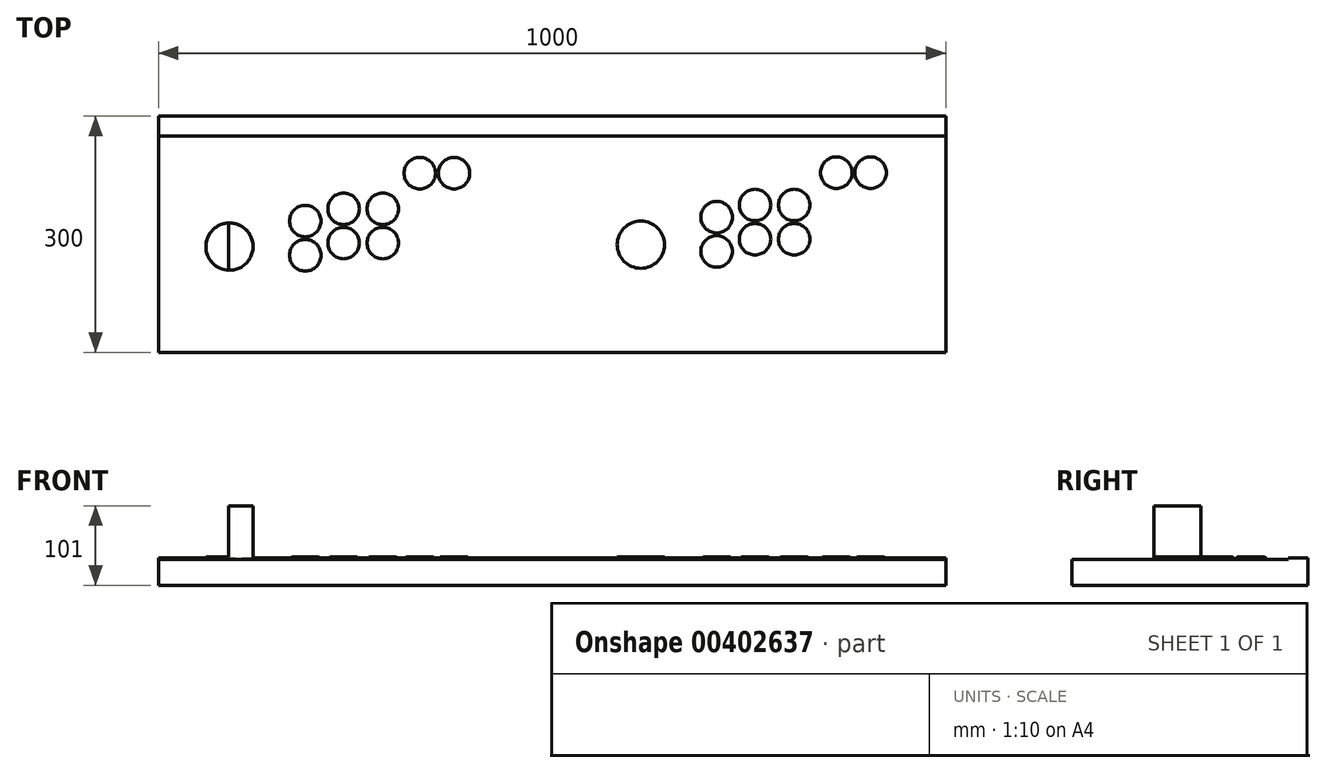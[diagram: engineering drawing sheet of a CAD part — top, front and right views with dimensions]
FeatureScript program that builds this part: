
annotation { "Feature Type Name" : "Feature", "Feature Type Description" : "" }
export const myFeature = defineFeature(function(context is Context, id is Id, definition is map)
    precondition{}
    {
        {
            var Q0;
            Q0=qCreatedBy(makeId("Front.planeOp"),FACE);
            var sketch = newSketch(context, id + "F0", { "sketchPlane" : qUnion([Q0])});
            skLineSegment(sketch, "E0.bottom", {"start": v(-84.86, 26.9) * mm, "end": v(915.14, 26.9) * mm});
            skLineSegment(sketch, "E0.top", {"start": v(-84.86, -8.1) * mm, "end": v(915.14, -8.1) * mm});
            skLineSegment(sketch, "E0.left", {"start": v(-84.86, 26.9) * mm, "end": v(-84.86, -8.1) * mm});
            skLineSegment(sketch, "E0.right", {"start": v(915.14, 26.9) * mm, "end": v(915.14, -8.1) * mm});
            skSolve(sketch);
        }
        {
            var Q0;
            Q0=makeQuery(id+"F0.imprint","IMPRINT",FACE,{"disambiguationData":[TD([[makeQuery(id+"F0.imprint","IMPRINT",EDGE,{"derivedFrom":sQuery(id+"F0.wireOp",EDGE,"E0.bottom")}),-1.0]])]});
            extrude(context, id + "F1", {"entities" : qUnion([Q0]), "depth" : 300 * mm});
        }
        {
            var Q0;
            Q0=makeQuery(id+"F1.opExtrude","SWEPT_FACE",FACE,{"disambiguationData":[OSD([sQuery(id+"F0.wireOp",EDGE,"E0.bottom")])]});
            var sketch = newSketch(context, id + "F2", { "sketchPlane" : qUnion([Q0])});
            skLineSegment(sketch, "E1", {"start": v(-84.86, 0) * mm, "end": v(-84.86, -25) * mm});
            skLineSegment(sketch, "E2", {"start": v(-84.86, -25) * mm, "end": v(915.14, -25) * mm});
            skLineSegment(sketch, "E3", {"start": v(915.14, -25) * mm, "end": v(915.14, -300) * mm});
            skLineSegment(sketch, "E4", {"start": v(915.14, -300) * mm, "end": v(-84.86, -300) * mm});
            skLineSegment(sketch, "E5", {"start": v(-84.86, -300) * mm, "end": v(-84.86, -25) * mm});
            skSolve(sketch);
        }
        {
            var Q0;
            Q0=makeQuery(id+"F2.imprint","IMPRINT",FACE,{"disambiguationData":[TD([[makeQuery(id+"F2.imprint","IMPRINT",EDGE,{"derivedFrom":sQuery(id+"F2.wireOp",EDGE,"E2")}),-1.0]])]});
            extrude(context, id + "F3", {"entities" : qUnion([Q0]), "operationType" : NewBodyOperationType.REMOVE, "oppositeDirection" : true, "depth" : 2 * mm});
        }
        {
            var Q0;
            Q0=makeQuery(id+"F3.boolean.opBoolean","COPY",FACE,{"derivedFrom":makeQuery(id+"F3.opExtrude","CAP_FACE",FACE,{"disambiguationData":[OSD([sQuery(id+"F2.wireOp",EDGE,"E2"),sQuery(id+"F2.wireOp",EDGE,"E3"),sQuery(id+"F2.wireOp",EDGE,"E4"),sQuery(id+"F2.wireOp",EDGE,"E5")])],"isStart":false})});
            var sketch = newSketch(context, id + "F4", { "sketchPlane" : qUnion([Q0])});
            skCircle(sketch, "E6", {"center": v(101.57, -133.2) * mm, "radius": 20 * mm});
            skCircle(sketch, "E7", {"center": v(101.57, -176.72) * mm, "radius": 20 * mm});
            skCircle(sketch, "E8", {"center": v(150.29, -117.7) * mm, "radius": 20 * mm});
            skCircle(sketch, "E9", {"center": v(150.29, -161.2) * mm, "radius": 20 * mm});
            skCircle(sketch, "E10", {"center": v(200.06, -117.7) * mm, "radius": 20 * mm});
            skCircle(sketch, "E11", {"center": v(200.06, -161.2) * mm, "radius": 20 * mm});
            skCircle(sketch, "E12", {"center": v(624.16, -128.32) * mm, "radius": 20 * mm});
            skCircle(sketch, "E13", {"center": v(624.16, -171.83) * mm, "radius": 20 * mm});
            skCircle(sketch, "E14", {"center": v(672.88, -112.82) * mm, "radius": 20 * mm});
            skCircle(sketch, "E15", {"center": v(672.88, -156.32) * mm, "radius": 20 * mm});
            skCircle(sketch, "E16", {"center": v(722.66, -112.82) * mm, "radius": 20 * mm});
            skCircle(sketch, "E17", {"center": v(722.66, -156.32) * mm, "radius": 20 * mm});
            skCircle(sketch, "E18", {"center": v(5.32, -165.7) * mm, "radius": 30 * mm});
            skCircle(sketch, "E19", {"center": v(527.86, -163.26) * mm, "radius": 30 * mm});
            skCircle(sketch, "E20", {"center": v(247.04, -72.43) * mm, "radius": 20 * mm});
            skCircle(sketch, "E21", {"center": v(290.54, -72.43) * mm, "radius": 20 * mm});
            skCircle(sketch, "E22", {"center": v(776.15, -71.82) * mm, "radius": 20 * mm});
            skCircle(sketch, "E23", {"center": v(819.66, -71.82) * mm, "radius": 20 * mm});
            skSolve(sketch);
        }
        {
            var Q0;
            Q0=makeQuery(id+"F4.imprint","IMPRINT",FACE,{"disambiguationData":[TD([[makeQuery(id+"F4.imprint","IMPRINT",EDGE,{"derivedFrom":sQuery(id+"F4.wireOp",EDGE,"E18")}),1.0]])]});
            var Q1;
            Q1=makeQuery(id+"F4.imprint","IMPRINT",FACE,{"disambiguationData":[TD([[makeQuery(id+"F4.imprint","IMPRINT",EDGE,{"derivedFrom":sQuery(id+"F4.wireOp",EDGE,"E7")}),1.0]])]});
            var Q2;
            Q2=makeQuery(id+"F4.imprint","IMPRINT",FACE,{"disambiguationData":[TD([[makeQuery(id+"F4.imprint","IMPRINT",EDGE,{"derivedFrom":sQuery(id+"F4.wireOp",EDGE,"E6")}),1.0]])]});
            var Q3;
            Q3=makeQuery(id+"F4.imprint","IMPRINT",FACE,{"disambiguationData":[TD([[makeQuery(id+"F4.imprint","IMPRINT",EDGE,{"derivedFrom":sQuery(id+"F4.wireOp",EDGE,"E8")}),1.0]])]});
            var Q4;
            Q4=makeQuery(id+"F4.imprint","IMPRINT",FACE,{"disambiguationData":[TD([[makeQuery(id+"F4.imprint","IMPRINT",EDGE,{"derivedFrom":sQuery(id+"F4.wireOp",EDGE,"E11")}),1.0]])]});
            var Q5;
            Q5=makeQuery(id+"F4.imprint","IMPRINT",FACE,{"disambiguationData":[TD([[makeQuery(id+"F4.imprint","IMPRINT",EDGE,{"derivedFrom":sQuery(id+"F4.wireOp",EDGE,"E10")}),1.0]])]});
            var Q6;
            Q6=makeQuery(id+"F4.imprint","IMPRINT",FACE,{"disambiguationData":[TD([[makeQuery(id+"F4.imprint","IMPRINT",EDGE,{"derivedFrom":sQuery(id+"F4.wireOp",EDGE,"E9")}),1.0]])]});
            var Q7;
            Q7=makeQuery(id+"F4.imprint","IMPRINT",FACE,{"disambiguationData":[TD([[makeQuery(id+"F4.imprint","IMPRINT",EDGE,{"derivedFrom":sQuery(id+"F4.wireOp",EDGE,"E20")}),1.0]])]});
            var Q8;
            Q8=makeQuery(id+"F4.imprint","IMPRINT",FACE,{"disambiguationData":[TD([[makeQuery(id+"F4.imprint","IMPRINT",EDGE,{"derivedFrom":sQuery(id+"F4.wireOp",EDGE,"E21")}),1.0]])]});
            var Q9;
            Q9=makeQuery(id+"F4.imprint","IMPRINT",FACE,{"disambiguationData":[TD([[makeQuery(id+"F4.imprint","IMPRINT",EDGE,{"derivedFrom":sQuery(id+"F4.wireOp",EDGE,"E19")}),1.0]])]});
            var Q10;
            Q10=makeQuery(id+"F4.imprint","IMPRINT",FACE,{"disambiguationData":[TD([[makeQuery(id+"F4.imprint","IMPRINT",EDGE,{"derivedFrom":sQuery(id+"F4.wireOp",EDGE,"E13")}),1.0]])]});
            var Q11;
            Q11=makeQuery(id+"F4.imprint","IMPRINT",FACE,{"disambiguationData":[TD([[makeQuery(id+"F4.imprint","IMPRINT",EDGE,{"derivedFrom":sQuery(id+"F4.wireOp",EDGE,"E12")}),1.0]])]});
            var Q12;
            Q12=makeQuery(id+"F4.imprint","IMPRINT",FACE,{"disambiguationData":[TD([[makeQuery(id+"F4.imprint","IMPRINT",EDGE,{"derivedFrom":sQuery(id+"F4.wireOp",EDGE,"E14")}),1.0]])]});
            var Q13;
            Q13=makeQuery(id+"F4.imprint","IMPRINT",FACE,{"disambiguationData":[TD([[makeQuery(id+"F4.imprint","IMPRINT",EDGE,{"derivedFrom":sQuery(id+"F4.wireOp",EDGE,"E15")}),1.0]])]});
            var Q14;
            Q14=makeQuery(id+"F4.imprint","IMPRINT",FACE,{"disambiguationData":[TD([[makeQuery(id+"F4.imprint","IMPRINT",EDGE,{"derivedFrom":sQuery(id+"F4.wireOp",EDGE,"E17")}),1.0]])]});
            var Q15;
            Q15=makeQuery(id+"F4.imprint","IMPRINT",FACE,{"disambiguationData":[TD([[makeQuery(id+"F4.imprint","IMPRINT",EDGE,{"derivedFrom":sQuery(id+"F4.wireOp",EDGE,"E16")}),1.0]])]});
            var Q16;
            Q16=makeQuery(id+"F4.imprint","IMPRINT",FACE,{"disambiguationData":[TD([[makeQuery(id+"F4.imprint","IMPRINT",EDGE,{"derivedFrom":sQuery(id+"F4.wireOp",EDGE,"E22")}),1.0]])]});
            var Q17;
            Q17=makeQuery(id+"F4.imprint","IMPRINT",FACE,{"disambiguationData":[TD([[makeQuery(id+"F4.imprint","IMPRINT",EDGE,{"derivedFrom":sQuery(id+"F4.wireOp",EDGE,"E23")}),1.0]])]});
            extrude(context, id + "F5", {"entities" : qUnion([Q0, Q1, Q2, Q3, Q4, Q5, Q6, Q7, Q8, Q9, Q10, Q11, Q12, Q13, Q14, Q15, Q16, Q17]), "operationType" : NewBodyOperationType.ADD, "depth" : 3 * mm});
        }
        {
            var Q0;
            Q0=makeQuery(id+"F5.opExtrude","CAP_EDGE",EDGE,{"disambiguationData":[OSD([sQuery(id+"F4.wireOp",EDGE,"E7")])],"isStart":false});
            var Q1;
            Q1=makeQuery(id+"F5.opExtrude","CAP_FACE",FACE,{"disambiguationData":[OSD([sQuery(id+"F4.wireOp",EDGE,"E6")])],"isStart":false});
            var Q2;
            Q2=makeQuery(id+"F5.opExtrude","CAP_FACE",FACE,{"disambiguationData":[OSD([sQuery(id+"F4.wireOp",EDGE,"E8")])],"isStart":false});
            var Q3;
            Q3=makeQuery(id+"F5.opExtrude","CAP_FACE",FACE,{"disambiguationData":[OSD([sQuery(id+"F4.wireOp",EDGE,"E9")])],"isStart":false});
            var Q4;
            Q4=makeQuery(id+"F5.opExtrude","CAP_FACE",FACE,{"disambiguationData":[OSD([sQuery(id+"F4.wireOp",EDGE,"E11")])],"isStart":false});
            var Q5;
            Q5=makeQuery(id+"F5.opExtrude","CAP_FACE",FACE,{"disambiguationData":[OSD([sQuery(id+"F4.wireOp",EDGE,"E10")])],"isStart":false});
            var Q6;
            Q6=makeQuery(id+"F5.opExtrude","CAP_FACE",FACE,{"disambiguationData":[OSD([sQuery(id+"F4.wireOp",EDGE,"E20")])],"isStart":false});
            var Q7;
            Q7=makeQuery(id+"F5.opExtrude","CAP_FACE",FACE,{"disambiguationData":[OSD([sQuery(id+"F4.wireOp",EDGE,"E21")])],"isStart":false});
            var Q8;
            Q8=makeQuery(id+"F5.opExtrude","CAP_FACE",FACE,{"disambiguationData":[OSD([sQuery(id+"F4.wireOp",EDGE,"E23")])],"isStart":false});
            var Q9;
            Q9=makeQuery(id+"F5.opExtrude","CAP_FACE",FACE,{"disambiguationData":[OSD([sQuery(id+"F4.wireOp",EDGE,"E22")])],"isStart":false});
            var Q10;
            Q10=makeQuery(id+"F5.opExtrude","CAP_FACE",FACE,{"disambiguationData":[OSD([sQuery(id+"F4.wireOp",EDGE,"E16")])],"isStart":false});
            var Q11;
            Q11=makeQuery(id+"F5.opExtrude","CAP_FACE",FACE,{"disambiguationData":[OSD([sQuery(id+"F4.wireOp",EDGE,"E17")])],"isStart":false});
            var Q12;
            Q12=makeQuery(id+"F5.opExtrude","CAP_FACE",FACE,{"disambiguationData":[OSD([sQuery(id+"F4.wireOp",EDGE,"E15")])],"isStart":false});
            var Q13;
            Q13=makeQuery(id+"F5.opExtrude","CAP_FACE",FACE,{"disambiguationData":[OSD([sQuery(id+"F4.wireOp",EDGE,"E14")])],"isStart":false});
            var Q14;
            Q14=makeQuery(id+"F5.opExtrude","CAP_FACE",FACE,{"disambiguationData":[OSD([sQuery(id+"F4.wireOp",EDGE,"E12")])],"isStart":false});
            var Q15;
            Q15=makeQuery(id+"F5.opExtrude","CAP_FACE",FACE,{"disambiguationData":[OSD([sQuery(id+"F4.wireOp",EDGE,"E13")])],"isStart":false});
            fillet(context, id + "F6", {"entities" : qUnion([Q0, Q1, Q2, Q3, Q4, Q5, Q6, Q7, Q8, Q9, Q10, Q11, Q12, Q13, Q14, Q15]), "radius" : 5 * mm, "tangentPropagation" : true, "allowEdgeOverflow" : false});
        }
        {
            var Q0;
            Q0=makeQuery(id+"F5.opExtrude","CAP_FACE",FACE,{"disambiguationData":[OSD([sQuery(id+"F4.wireOp",EDGE,"E18")])],"isStart":false});
            var sketch = newSketch(context, id + "F7", { "sketchPlane" : qUnion([Q0])});
            skLineSegment(sketch, "E24", {"start": v(-24.68, -165.94) * mm, "end": v(35.31, -165.94) * mm});
            skLineSegment(sketch, "E25", {"start": v(4.43, -135.7) * mm, "end": v(4.43, -195.68) * mm});
            skLineSegment(sketch, "E26", {"start": v(526.33, -132.92) * mm, "end": v(526.33, -192.14) * mm});
            skLineSegment(sketch, "E27", {"start": v(557.47, -162.22) * mm, "end": v(497.03, -162.22) * mm});
            skCircle(sketch, "E28", {"center": v(4.43, -165.94) * mm, "radius": 10 * mm});
            skCircle(sketch, "E29", {"center": v(527.25, -162.22) * mm, "radius": 10 * mm});
            skSolve(sketch);
        }
        {
            var Q0;
            {var subQ0=sQuery(id+"F7.wireOp",EDGE,"E25");var subQ1=sQuery(id+"F7.wireOp",EDGE,"E24");var subQ2=makeQuery(id+"F7.imprint","INTERSECT",VERTEX,{"derivedFrom":[subQ1,subQ0]});Q0=makeQuery(id+"F7.imprint","IMPRINT",FACE,{"disambiguationData":[TD([[makeQuery(id+"F7.imprint","IMPRINT",EDGE,{"disambiguationData":[TD([[subQ2,-1.0]])],"derivedFrom":subQ1}),-1.0]])]});}
            var Q1;
            {var subQ0=sQuery(id+"F7.wireOp",EDGE,"E28");var subQ1=sQuery(id+"F7.wireOp",EDGE,"E24");var subQ2=makeQuery(id+"F7.imprint","INTERSECT",VERTEX,{"disambiguationData":[OD(0.0)],"derivedFrom":[subQ1,subQ0]});Q1=makeQuery(id+"F7.imprint","IMPRINT",FACE,{"disambiguationData":[TD([[makeQuery(id+"F7.imprint","IMPRINT",EDGE,{"disambiguationData":[TD([[subQ2,-1.0]])],"derivedFrom":subQ1}),-1.0]])]});}
            var Q2;
            {var subQ0=sQuery(id+"F7.wireOp",EDGE,"E28");var subQ1=sQuery(id+"F7.wireOp",EDGE,"E24");var subQ2=makeQuery(id+"F7.imprint","INTERSECT",VERTEX,{"disambiguationData":[OD(0.0)],"derivedFrom":[subQ1,subQ0]});Q2=makeQuery(id+"F7.imprint","IMPRINT",FACE,{"disambiguationData":[TD([[makeQuery(id+"F7.imprint","IMPRINT",EDGE,{"disambiguationData":[TD([[subQ2,-1.0]])],"derivedFrom":subQ1}),1.0]])]});}
            var Q3;
            {var subQ0=sQuery(id+"F7.wireOp",EDGE,"E25");var subQ1=sQuery(id+"F7.wireOp",EDGE,"E24");var subQ2=makeQuery(id+"F7.imprint","INTERSECT",VERTEX,{"derivedFrom":[subQ1,subQ0]});Q3=makeQuery(id+"F7.imprint","IMPRINT",FACE,{"disambiguationData":[TD([[makeQuery(id+"F7.imprint","IMPRINT",EDGE,{"disambiguationData":[TD([[subQ2,-1.0]])],"derivedFrom":subQ1}),1.0]])]});}
            var Q4;
            {var subQ0=sQuery(id+"F7.wireOp",EDGE,"E29");var subQ1=sQuery(id+"F7.wireOp",EDGE,"E26");var subQ2=makeQuery(id+"F7.imprint","INTERSECT",VERTEX,{"disambiguationData":[OD(1.0)],"derivedFrom":[subQ1,subQ0]});Q4=makeQuery(id+"F7.imprint","IMPRINT",FACE,{"disambiguationData":[TD([[makeQuery(id+"F7.imprint","IMPRINT",EDGE,{"disambiguationData":[TD([[subQ2,1.0]])],"derivedFrom":subQ1}),1.0]])]});}
            var Q5;
            {var subQ0=sQuery(id+"F7.wireOp",EDGE,"E29");var subQ1=sQuery(id+"F7.wireOp",EDGE,"E26");var subQ2=makeQuery(id+"F7.imprint","INTERSECT",VERTEX,{"disambiguationData":[OD(1.0)],"derivedFrom":[subQ1,subQ0]});Q5=makeQuery(id+"F7.imprint","IMPRINT",FACE,{"disambiguationData":[TD([[makeQuery(id+"F7.imprint","IMPRINT",EDGE,{"disambiguationData":[TD([[subQ2,1.0]])],"derivedFrom":subQ1}),-1.0]])]});}
            var Q6;
            {var subQ0=sQuery(id+"F7.wireOp",EDGE,"E29");var subQ1=sQuery(id+"F7.wireOp",EDGE,"E26");var subQ2=makeQuery(id+"F7.imprint","INTERSECT",VERTEX,{"disambiguationData":[OD(0.0)],"derivedFrom":[subQ1,subQ0]});Q6=makeQuery(id+"F7.imprint","IMPRINT",FACE,{"disambiguationData":[TD([[makeQuery(id+"F7.imprint","IMPRINT",EDGE,{"disambiguationData":[TD([[subQ2,-1.0]])],"derivedFrom":subQ1}),-1.0]])]});}
            var Q7;
            {var subQ0=sQuery(id+"F7.wireOp",EDGE,"E29");var subQ1=sQuery(id+"F7.wireOp",EDGE,"E26");var subQ2=makeQuery(id+"F7.imprint","INTERSECT",VERTEX,{"disambiguationData":[OD(0.0)],"derivedFrom":[subQ1,subQ0]});Q7=makeQuery(id+"F7.imprint","IMPRINT",FACE,{"disambiguationData":[TD([[makeQuery(id+"F7.imprint","IMPRINT",EDGE,{"disambiguationData":[TD([[subQ2,-1.0]])],"derivedFrom":subQ1}),1.0]])]});}
            extrude(context, id + "F8", {"entities" : qUnion([Q0, Q1, Q2, Q3, Q4, Q5, Q6, Q7]), "operationType" : NewBodyOperationType.ADD, "depth" : 65 * mm});
        }
    });
